# Revit family: equip-sink-elkay-sta-wall-ewma9620stmc
name_source: partatom
category: Plumbing Fixtures
units: mm (PartAtom-declared; Revit-internal decimal feet)

## family parameters
Cut with Voids When Loaded = No
Host = Face
Part Type = Normal
Room Calculation Point = No
Round Connector Dimension = Use Radius
Shared = No

## types (2) — shared parameters
Angle to Drain = 90.00°
Assembly Code = D2010410
Backsplash Height = 0' - 10"
Backsplash Width = 0' - 2"
Bowl Depth = 0' - 8"
Bowl Drain Location FB = 0' - 6 7/8"
Bowl Length = 7' - 8 1/2"
Bowl Width = 1' - 1 3/4"
Bracket Front from Wall = 1' - 2"
Bubbler CW Flow Rate = 2 GPM
Bubbler Material = Metal - Steel - Stainless - Chrome
Bubbler Nominal Dia = 0' - 0 1/2"
Bubbler Nominal Radius = 0' - 0 1/4"
CW Flow Rate = 2 GPM
Cost = 1 $
Default Elevation = 3' - 0"
Description = Wash-Up Lavatory Sinks
Drain CL LR to Left Bowl Edge = 3' - 10 1/4"
Drain Material = Metal - Steel - Stainless - Chrome
Drain Pipe Extension = 0' - 1 11/16"
Faucet 1 Hole A Front = 0' - 0 1/4"
Faucet 1 Hole A to B = 0' - 2"
Faucet 1 Hole A to Rough-In Water Supply CL 1 = 0' - 0"
Faucet 1 Hole B Front = 0' - 0 1/8"
Faucet 2 CL Horiz to Valve Inlet CL = 0' - 0 1/16"
Faucet 2 Hole A From CL = 1' - 2"
Faucet 2 Hole A Front = 0' - 0 1/8"
Faucet 2 Hole B Front = 0' - 0 1/4"
Faucet 2 Hole B from Hole A = 0' - 2"
Faucet 2 Hole B to CL Sink = 1' - 0"
Faucet 2 Hole B to Rough-In Water Supply CL 2 = 0' - 0"
Faucet 3 CL Horiz to Valve Inlet CL = 0' - 0 1/16"
Faucet 3 Hole A Front = 0' - 0 1/8"
Faucet 3 Hole B to A = 0' - 2"
Faucet 3 Hole B to Rough-In Water Supply CL 3 = 0' - 0"
Faucet 3 Hole B to Sink CL = 1' - 0"
Faucet 4 CL to CL AC Adapter 4 = 0' - 7"
Faucet 4 Hole A Front = 0' - 0 1/8"
Faucet 4 Hole B Front = 0' - 0 1/4"
Faucet 4 Hole B to A = 0' - 2"
Faucet 4 Hole B to Rough-In Water Supply CL 4 = 0' - 0"
Faucet CL Horiz to Control Box Inlet = 0' - 1 5/8"
Faucet CL Horiz to Valve Inlet CL = 0' - 0 1/16"
Faucet CL Vert to Bottom of Control Box Inlet = 2' - 2 11/32"
Faucet CL to AC Adapter = 0' - 7"
Faucet CL to AC Adapter Elev = 1' - 10"
Faucet CL to Top Backsplash = 0' - 4"
Faucet CL to Wall = 0' - 3"
Faucet Hole Dia = 0' - 1 1/2"
Faucet Hole One = No
Faucet Hole Three = No
Faucet Hole Two = Yes
Faucet Material = Metal - Steel - Stainless - Chrome
Faucet Part = LKB722C
Faucet Water Supply Radius = 0' - 0 3/16"
HW Flow Rate = 2 GPM
Hidden Length = 8' - 0"
Hidden Width = 1' - 8"
Hole Radius = 0' - 0 3/4"
Keynote = D2010410
Manufacturer = Elkay Manufacturing
MasterFormat Number = 22.42.16.16
MasterFormat Title = Commercial Sinks
Mechanical Mix Valve = No
Mix Valve Part = LK723
No Mix Valve = No
Nominal Dia = 0' - 0 1/2"
Nominal Radius = 0' - 0 1/4"
OmniClass Code = 23.45.05.14.14.27
OmniClass Title = Service Sinks
Rough-In Sanitary Installation Height = 1' - 11"
Rough-In Sanitary Right From CL Sink = 0' - 0"
Rough-In Water Supply CL Separation = 0' - 8"
Rough-In Water Supply Installation Height = 0' - 8 5/8"
Sanitary Flow Rate = 10 GPM
Sanitary Nominal Dia = 0' - 1 1/2"
Sanitary Nominal Radius = 0' - 0 3/4"
Side Splashes = No
Sink Bottom Corner From Front = 0' - 4 1/4"
Sink Edge Left to Faucet 1 Hole A = 1' - 0"
Sink Edge Right to Faucet 4 Hole B = 1' - 0"
Sink Length = 8' - 0"
Sink Material = Metal - Steel - Stainless - Chrome
Sink Part = EWMA96203
Sink Rim Front Width = 0' - 1 1/2"
Sink Rim Left Width = 0' - 1 1/2"
Sink Rim Right Width = 0' - 1 1/2"
Sink San Conn Extr Visibility = No
Sink Width = 1' - 8"
Specification Sheet URL = http://www.elkayusa.com
Stem Material = Metal - Steel
Supply Line Mix Length = 0' - 0 1/2"
Thermostatic Mix Valve = Yes
URL = www.elkayusa.com
Valve Material = Metal - Brass
Vent Connection = Yes
zero-valued in all types: CWFU, HWFU, WFU

## per-type parameters (varying)
| type | AC Power | Faucet 3 Hole B Front | Faucet 3 Hole B from CL |
| EWMA9620SACTMC | Yes | 0' - 0 1/8" | 0' - 4" |
| EWMA9620SBTMC | No | 0' - 0 1/4" | 1' - 0" |

note: column(s) folded — value = type name in every type: Model

## geometry (parser evidence)
native form markers: Sweep x16
no freeform markers — native parametric forms only
